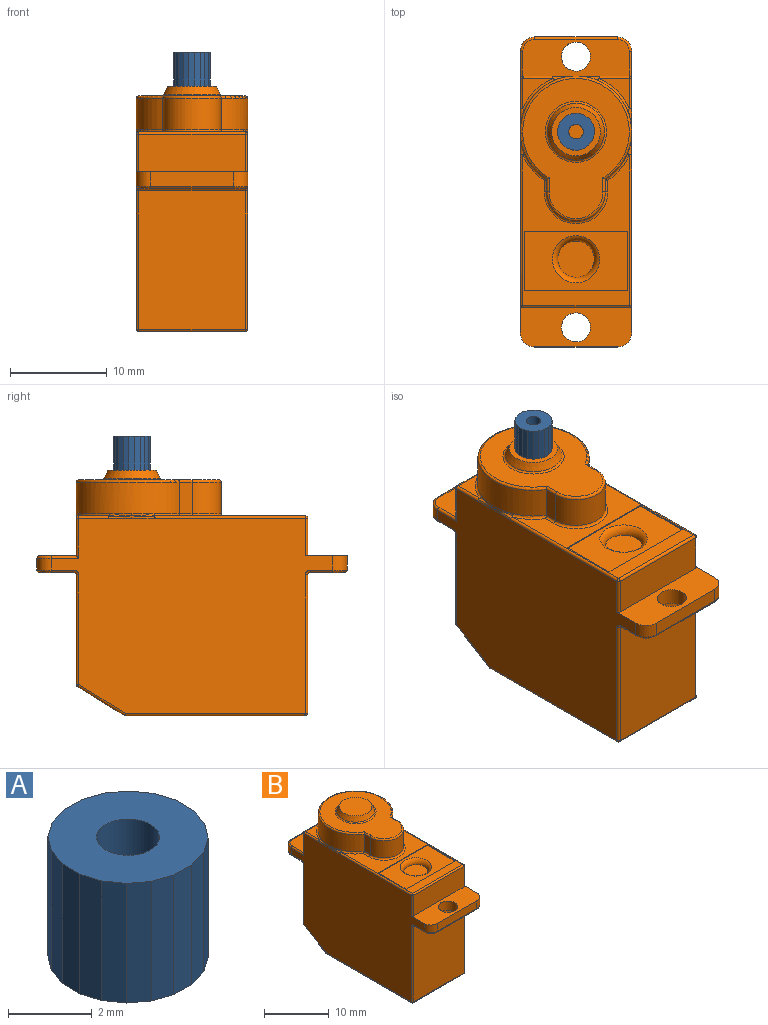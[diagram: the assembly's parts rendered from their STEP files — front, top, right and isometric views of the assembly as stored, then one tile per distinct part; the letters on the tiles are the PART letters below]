
ASSEMBLY  parts=2 mates=1
PART A: 23 faces, bbox 3.8x3.8x3.5 mm
  f0: plane 3.5x0.57mm, normal (0.33,0.95,0), area 2.1mm2, adj f1,f19,f21,f22
  f1: plane 3.5x0.6mm, normal (0.02,1,0), area 2.1mm2, adj f0,f2,f21,f22
  f2: plane 3.5x0.57mm, normal (-0.29,0.96,0), area 2.1mm2, adj f1,f3,f21,f22
  f3: plane 3.5x0.49mm, normal (-0.57,0.82,0), area 2.1mm2, adj f2,f4,f21,f22
  f4: plane 3.5x0.48mm, normal (-0.8,0.6,0), area 2.1mm2, adj f3,f5,f21,f22
  f5: plane 3.5x0.57mm, normal (-0.95,0.33,0), area 2.1mm2, adj f4,f6,f21,f22
  f6: plane 3.5x0.6mm, normal (-1,0.02,0), area 2.1mm2, adj f5,f7,f21,f22
  f7: plane 3.5x0.57mm, normal (-0.96,-0.29,0), area 2.1mm2, adj f6,f8,f21,f22
  f8: plane 3.5x0.49mm, normal (-0.82,-0.57,0), area 2.1mm2, adj f7,f9,f21,f22
  f9: plane 3.5x0.48mm, normal (-0.6,-0.8,0), area 2.1mm2, adj f8,f10,f21,f22
  f10: plane 3.5x0.57mm, normal (-0.33,-0.95,0), area 2.1mm2, adj f9,f11,f21,f22
  f11: plane 3.5x0.6mm, normal (-0.02,-1,0), area 2.1mm2, adj f10,f12,f21,f22
  f12: plane 3.5x0.57mm, normal (0.29,-0.96,0), area 2.1mm2, adj f11,f13,f21,f22
  f13: plane 3.5x0.49mm, normal (0.57,-0.82,0), area 2.1mm2, adj f12,f14,f21,f22
  f14: plane 3.5x0.48mm, normal (0.8,-0.6,0), area 2.1mm2, adj f13,f15,f21,f22
  f15: plane 3.5x0.57mm, normal (0.95,-0.33,0), area 2.1mm2, adj f14,f16,f21,f22
  f16: plane 3.5x0.6mm, normal (1,-0.02,0), area 2.1mm2, adj f15,f17,f21,f22
  f17: plane 3.5x0.57mm, normal (0.96,0.29,0), area 2.1mm2, adj f16,f18,f21,f22
  f18: plane 3.5x0.49mm, normal (0.82,0.57,0), area 2.1mm2, adj f17,f19,f21,f22
  f19: plane 3.5x0.48mm, normal (0.6,0.8,0), area 2.1mm2, adj f0,f18,f21,f22
  f20: cylinder r=0.75mm len=3.5mm, axis (0,0,-1), area 16.5mm2, adj f21,f22
  f21: plane 3.79x3.79mm, normal (0,0,1), area 9.5mm2, adj f0,f1,f2,f3,f4,f5,f6,f7
  f22: plane 3.79x3.79mm, normal (0,0,-1), area 9.5mm2, adj f0,f1,f2,f3,f4,f5,f6,f7
PART B: 120 faces, bbox 12.4x32.2x25.3 mm
  f0: plane 15.5x11mm, normal (0,0,1), area 56.5mm2, adj f22,f23,f24,f25,f83,f86,f87,f88
  f1: plane 3.11x3.1mm, normal (0,0,1), area 3.6mm2, adj f98,f105,f106
  f2: plane 18.56x11mm, normal (0,0,-1), area 204.1mm2, adj f45,f48,f49,f50
  f3: plane 11x4.82mm, normal (0,0.53,-0.85), area 62.4mm2, adj f50,f53,f54,f55
  f4: plane 11.28x11mm, normal (0,1,0), area 124.1mm2, adj f55,f58,f59,f60
  f5: plane 11x3.54mm, normal (0,0,-1), area 31.2mm2, adj f30,f60,f63,f64,f65,f66,f67
  f6: plane 8.5x1.22mm, normal (0,1,0), area 10.4mm2, adj f32,f34,f67,f109
  f7: plane 11x3.79mm, normal (0,0,1), area 34mm2, adj f8,f30,f104,f107,f109,f111,f112
  f8: plane 11x3.86mm, normal (0,1,0), area 42.5mm2, adj f7,f76,f77,f96,f101,f105,f110
  f9: plane 3.11x3.1mm, normal (0,0,1), area 3.6mm2, adj f91,f96,f97
  f10: plane 11x3.86mm, normal (0,-1,0), area 42.5mm2, adj f11,f84,f89,f90
  f11: plane 11.5x4.29mm, normal (0,0,1), area 38.5mm2, adj f10,f12,f15,f16,f29,f31,f33,f84
  f12: plane 8.5x1.47mm, normal (0,-1,0), area 12.5mm2, adj f11,f31,f33,f35
  f13: plane 11x3.54mm, normal (0,0,-1), area 31.2mm2, adj f29,f35,f36,f37,f38,f39,f40
  f14: plane 14.27x11mm, normal (0,-1,0), area 157mm2, adj f40,f43,f44,f45
  f15: plane 28.96x20.1mm, normal (1,0,0), area 470.3mm2, adj f11,f33,f34,f38,f41,f43,f48,f53
  f16: plane 28.96x20.1mm, normal (-1,0,0), area 470.3mm2, adj f11,f31,f32,f39,f42,f44,f49,f54
  f17: plane 3.22x1.31mm, normal (-1,0,0), area 4.2mm2, adj f18,f20,f93,f113
  f18: cylinder r=3.02mm len=6.04mm, axis (0,0,-1), area 30.6mm2, adj f17,f19,f88,f114
  f19: plane 3.22x1.31mm, normal (1,0,0), area 4.2mm2, adj f18,f20,f83,f116
  f20: cylinder r=5.75mm len=11.49mm, axis (0,0,-1), area 95.8mm2, adj f17,f19,f70,f71,f73,f74,f78,f87
  f21: plane 14.46x10.99mm, normal (0,0,1), area 80.9mm2, adj f113,f114,f115,f116,f119
  f22: plane 6.1x0.1mm, normal (-1,0,0), area 0.6mm2, adj f0,f23,f25,f26
  f23: plane 10.7x0.1mm, normal (0,-1,0), area 1.1mm2, adj f0,f22,f24,f26
  f24: plane 6.1x0.1mm, normal (1,0,0), area 0.6mm2, adj f0,f23,f25,f26
  f25: plane 10.7x0.1mm, normal (0,1,0), area 1.1mm2, adj f0,f22,f24,f26
  f26: plane 10.7x6.1mm, normal (0,0,1), area 46.6mm2, adj f22,f23,f24,f25,f28
  f27: plane 3.75x3.75mm, normal (0,0,1), area 11mm2, adj f28
  f28: torus R=2.88mm, axis (0,0,1), area 14.6mm2, adj f26,f27
  f29: cylinder r=1.5mm len=3mm, axis (0,0,1), area 16.2mm2, adj f11,f13
  f30: cylinder r=1.5mm len=3mm, axis (0,0,1), area 16.2mm2, adj f5,f7
  f31: cylinder r=1.5mm len=1.5mm, axis (0,0,-1), area 3.5mm2, adj f11,f12,f16,f37
  f32: cylinder r=1.5mm len=1.5mm, axis (0,0,1), area 2.9mm2, adj f6,f16,f66,f111
  f33: cylinder r=1.5mm len=1.5mm, axis (0,0,1), area 3.5mm2, adj f11,f12,f15,f36
  f34: cylinder r=1.5mm len=1.5mm, axis (0,0,-1), area 2.9mm2, adj f6,f15,f65,f107
  f35: cylinder r=0.25mm len=8.5mm, axis (-1,0,0), area 3.3mm2, adj f12,f13,f36,f37
  f36: torus R=1.25mm, axis (0,0,-1), area 0.9mm2, adj f13,f33,f35,f38
  f37: torus R=1.25mm, axis (0,0,-1), area 0.9mm2, adj f13,f31,f35,f39
  f38: cylinder r=0.25mm len=2.29mm, axis (0,-1,0), area 0.9mm2, adj f13,f15,f36,f41
  f39: cylinder r=0.25mm len=2.29mm, axis (0,1,0), area 0.9mm2, adj f13,f16,f37,f42
  f40: cylinder r=0.25mm len=11mm, axis (-1,0,0), area 4.3mm2, adj f13,f14,f41,f42
  f41: torus R=0.5mm, axis (1,0,0), area 0.2mm2, adj f15,f38,f40,f43
  f42: torus R=0.5mm, axis (1,0,0), area 0.2mm2, adj f16,f39,f40,f44
  f43: cylinder r=0.25mm len=14.27mm, axis (0,0,1), area 5.6mm2, adj f14,f15,f41,f46
  f44: cylinder r=0.25mm len=14.27mm, axis (0,0,-1), area 5.6mm2, adj f14,f16,f42,f47
  f45: cylinder r=0.25mm len=11mm, axis (1,0,0), area 4.3mm2, adj f2,f14,f46,f47
  f46: sphere r=0.25mm, area 0.1mm2, adj f43,f45,f48
  f47: sphere r=0.25mm, area 0.1mm2, adj f44,f45,f49
  f48: cylinder r=0.25mm len=18.56mm, axis (0,-1,0), area 7.3mm2, adj f2,f15,f46,f51
  f49: cylinder r=0.25mm len=18.56mm, axis (0,1,0), area 7.3mm2, adj f2,f16,f47,f52
  f50: cylinder r=0.25mm len=11mm, axis (1,0,0), area 1.5mm2, adj f2,f3,f51,f52
  f51: sphere r=0.25mm, area 0mm2, adj f48,f50,f53
  f52: sphere r=0.25mm, area 0mm2, adj f49,f50,f54
  f53: cylinder r=0.25mm len=4.95mm, axis (0,-0.85,-0.53), area 2.2mm2, adj f3,f15,f51,f56
  f54: cylinder r=0.25mm len=4.95mm, axis (0,0.85,0.53), area 2.2mm2, adj f3,f16,f52,f57
  f55: cylinder r=0.25mm len=11mm, axis (1,0,0), area 2.8mm2, adj f3,f4,f56,f57
  f56: sphere r=0.25mm, area 0mm2, adj f53,f55,f58
  f57: sphere r=0.25mm, area 0mm2, adj f54,f55,f59
  f58: cylinder r=0.25mm len=11.28mm, axis (0,0,-1), area 4.4mm2, adj f4,f15,f56,f61
  f59: cylinder r=0.25mm len=11.28mm, axis (0,0,1), area 4.4mm2, adj f4,f16,f57,f62
  f60: cylinder r=0.25mm len=11mm, axis (-1,0,0), area 4.3mm2, adj f4,f5,f61,f62
  f61: torus R=0.5mm, axis (1,0,0), area 0.2mm2, adj f15,f58,f60,f63
  f62: torus R=0.5mm, axis (1,0,0), area 0.2mm2, adj f16,f59,f60,f64
  f63: cylinder r=0.25mm len=2.29mm, axis (0,-1,0), area 0.9mm2, adj f5,f15,f61,f65
  f64: cylinder r=0.25mm len=2.29mm, axis (0,1,0), area 0.9mm2, adj f5,f16,f62,f66
  f65: torus R=1.25mm, axis (0,0,1), area 0.9mm2, adj f5,f34,f63,f67
  f66: torus R=1.25mm, axis (0,0,1), area 0.9mm2, adj f5,f32,f64,f67
  f67: cylinder r=0.25mm len=8.5mm, axis (1,0,0), area 3.3mm2, adj f5,f6,f65,f66
  f68: bspline ~2.39x0.25mm, area 0.5mm2, adj f16,f69,f100,f103
  f69: bspline ~2.39x0.4mm, area 0.4mm2, adj f68,f70,f99,f100
  f70: bspline ~2.3x0.48mm, area 0.4mm2, adj f20,f69,f71,f99
  f71: bspline ~2.3x0.48mm, area 0.4mm2, adj f20,f70,f72,f98
  f72: bspline ~2.39x0.4mm, area 0.4mm2, adj f71,f98,f103,f106
  f73: bspline ~2.31x0.48mm, area 0.4mm2, adj f20,f74,f98,f102
  f74: bspline ~2.31x0.48mm, area 0.4mm2, adj f20,f73,f75,f97
  f75: bspline ~2.4x0.41mm, area 0.4mm2, adj f74,f76,f96,f97
  f76: bspline ~2.4x0.25mm, area 0.5mm2, adj f8,f75,f77,f96
  f77: bspline ~2.4x0.25mm, area 0.5mm2, adj f8,f76,f102,f105
  f78: bspline ~2.3x0.48mm, area 0.4mm2, adj f20,f79,f87,f92
  f79: bspline ~2.39x0.4mm, area 0.4mm2, adj f78,f80,f86,f87
  f80: bspline ~2.39x0.25mm, area 0.5mm2, adj f15,f79,f81,f86
  f81: bspline ~2.39x0.25mm, area 0.5mm2, adj f15,f80,f82,f91
  f82: bspline ~2.39x0.4mm, area 0.4mm2, adj f81,f91,f92,f97
  f83: cylinder r=0.25mm len=1.31mm, axis (0,1,0), area 0.5mm2, adj f0,f19,f87,f88
  f84: cylinder r=0.25mm len=3.86mm, axis (0,0,1), area 1.5mm2, adj f10,f11,f15,f85
  f85: sphere r=0.25mm, area 0.1mm2, adj f84,f86,f89
  f86: cylinder r=0.25mm len=15.51mm, axis (0,1,0), area 6.1mm2, adj f0,f15,f79,f80,f85
  f87: torus R=6mm, axis (0,0,1), area 1.4mm2, adj f0,f20,f78,f79,f83
  f88: torus R=3.27mm, axis (0,0,1), area 3.8mm2, adj f0,f18,f83,f93
  f89: cylinder r=0.25mm len=11mm, axis (-1,0,0), area 4.3mm2, adj f0,f10,f85,f94
  f90: cylinder r=0.25mm len=3.86mm, axis (0,0,-1), area 1.5mm2, adj f10,f11,f16,f94
  f91: cylinder r=0.25mm len=3.12mm, axis (0,1,0), area 1.2mm2, adj f9,f15,f81,f82,f95
  f92: bspline ~2.3x0.48mm, area 0.4mm2, adj f20,f78,f82,f97
  f93: cylinder r=0.25mm len=1.31mm, axis (0,-1,0), area 0.5mm2, adj f0,f17,f88,f99
  f94: sphere r=0.25mm, area 0.1mm2, adj f89,f90,f100
  f95: sphere r=0.25mm, area 0.1mm2, adj f91,f96,f101
  f96: cylinder r=0.25mm len=3.12mm, axis (-1,0,0), area 1.2mm2, adj f8,f9,f75,f76,f95
  f97: torus R=6mm, axis (0,0,1), area 1.7mm2, adj f9,f20,f74,f75,f82,f92
  f98: torus R=6mm, axis (0,0,1), area 1.7mm2, adj f1,f20,f71,f72,f73,f102
  f99: torus R=6mm, axis (0,0,1), area 1.4mm2, adj f0,f20,f69,f70,f93
  f100: cylinder r=0.25mm len=15.51mm, axis (0,-1,0), area 6.1mm2, adj f0,f16,f68,f69,f94
  f101: cylinder r=0.25mm len=4.11mm, axis (0,0,-1), area 1.6mm2, adj f8,f15,f95,f104
  f102: bspline ~2.4x0.41mm, area 0.4mm2, adj f73,f77,f98,f105
  f103: bspline ~2.39x0.25mm, area 0.5mm2, adj f16,f68,f72,f106
  f104: cylinder r=0.25mm len=2.79mm, axis (0,1,0), area 1mm2, adj f7,f15,f101,f107
  f105: cylinder r=0.25mm len=3.12mm, axis (-1,0,0), area 1.2mm2, adj f1,f8,f77,f102,f108
  f106: cylinder r=0.25mm len=3.12mm, axis (0,-1,0), area 1.2mm2, adj f1,f16,f72,f103,f108
  f107: torus R=1.25mm, axis (0,0,1), area 0.9mm2, adj f7,f34,f104,f109
  f108: sphere r=0.25mm, area 0.1mm2, adj f105,f106,f110
  f109: cylinder r=0.25mm len=8.5mm, axis (-1,0,0), area 3.3mm2, adj f6,f7,f107,f111
  f110: cylinder r=0.25mm len=4.11mm, axis (0,0,1), area 1.6mm2, adj f8,f16,f108,f112
  f111: torus R=1.25mm, axis (0,0,1), area 0.9mm2, adj f7,f32,f109,f112
  f112: cylinder r=0.25mm len=2.79mm, axis (0,-1,0), area 1mm2, adj f7,f16,f110,f111
  f113: cylinder r=0.25mm len=1.45mm, axis (0,1,0), area 0.5mm2, adj f17,f21,f114,f115
  f114: torus R=2.77mm, axis (0,0,1), area 3.6mm2, adj f18,f21,f113,f116
  f115: torus R=5.5mm, axis (0,0,1), area 11.5mm2, adj f20,f21,f113,f116
  f116: cylinder r=0.25mm len=1.45mm, axis (0,-1,0), area 0.5mm2, adj f19,f21,f114,f115
  f117: plane 5x5mm, normal (0,0,1), area 19.6mm2, adj f118
  f118: cone r=3mm half-angle=26.6deg, axis (0,0,-1), area 16.4mm2, adj f117,f119
  f119: torus R=3.15mm, axis (0,0,1), area 5.3mm2, adj f21,f118
PLACE A t=(-11.94,-6.39,6.53)mm
PLACE B t=(-11.94,-6.39,6.53)mm
MATE revolute B.f20 <-> A.f20  axis (0,0,1) through (-11.94,-0.19,21.51)mm
